# Revit family: HERZ измерительная диафрагма 4000_LF_MF
name_source: partatom
category: Rohrzubehör
units: mm (PartAtom-declared; Revit-internal decimal feet)

## family parameters
Arbeitsebenenbasiert = Nein
Beim Laden mit Abzugskörper schneiden = Nein
Bemaßung runder Anschluss = Durchmesser verwenden
Gemeinsam genutzt = Nein
Immer vertikal = Ja
OmniClass-Nummer = 23.65.55.14
OmniClass-Titel = Valves for Liquid Services
Teiletyp = Unterbricht

## types (2) — shared parameters
Hersteller = HERZ Armaturen Ges.m.b.H.
S03 = 10 mm  [stored 0.0328084 ft]
SCRNCODE = 02;01;02
SCRNSEQ = AWI;AWI_TYP="1001";02
URL = www.herz-armaturen.ru
Измерительные клапаны = латунь, CW602N
Исполнение = Корпус измерительной диафрагмы выполнен из латуни, устойчивой к селективной цинковой коррозии.
Два измерительных клапана встроены в диафрагму.
Согласно EN 10226 на входе в диафрагму - муфта с внутренней резьба Rp и на выходе - наружная резьба R.
Корпус = латунь, CC770S
Макс. рабочая температура (до DN32) = 130 °C
Макс. рабочая температура (от DN40) = 110 °C
Макс. рабочее давление = 2000000.0 Pa
Мин. рабочая температура = -20 °C
Применение = HERZ-измерительные диафрагмы устанавливаются на участках трубопроводов в системах отопления и холодоснабжения.
Измерительные диафрагмы могут устанавливаться как на подающей, так и на обратной линиях.
Они устанавливаются либо вплотную к HERZ балансировочному клапану, образуя комплект, либо используются вместе с HERZ запорным клапаном.
Участки балансируются с помощью настроек балансировочного клапана при измерении потери давления на измерительной диафрагме.
Среда = Качество теплоносителя в соответствии с ÖNORM H5195 и VDI 2035.
Допускается использование этилен- и пропиленгликоля в объемном соотношении 25-50 % с водой.
zero-valued in all types: Vorgabe-Ansicht

## per-type parameters (varying)
| type | LF | MF |
| LF | Ja | Nein |
| MF | Nein | Ja |

note: [stored X ft] marks values corroborated as IEEE doubles in the binary element streams (Revit-internal decimal feet)
